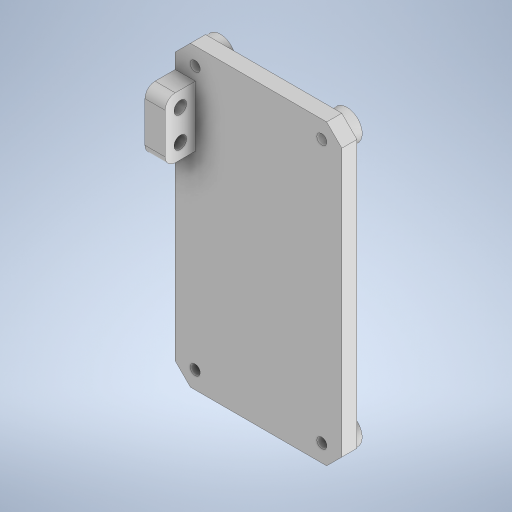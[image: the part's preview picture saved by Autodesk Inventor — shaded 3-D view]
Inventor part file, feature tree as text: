
AUTODESK INVENTOR PART (.ipt)
format: ipt  version: 2023 (Build 270158000, 158)  size: 288,256 bytes
history: native  units: mm
features: sketch x3, extrude x3, projected_geometry x3, other x1, hole x1, fillet x1, chamfer x1
ambient origin geometry x8: Origin, YZ Plane, XZ Plane, XY Plane, X Axis, Y Axis, Z Axis, Center Point
bodies: Body1 (feature_tree)
feature tree (13):
  other  "솔리드1"
  sketch  "스케치1"
  extrude  "돌출1"  Depth=33.0mm
  extrude  "돌출2"  Depth=59.0mm
  hole  "구멍1"  [1 undecoded]
  extrude  "돌출3"  Depth=57.6mm
  fillet  "모깎기1"  Radius=6.0mm
  chamfer  "모따기1"  Distance=25.1mm
  sketch  "스케치3"
  projected_geometry  "투영된 루프1"
  projected_geometry  "투영된 루프2"
  projected_geometry  "투영된 루프3"
  sketch  "스케치4"
note: 1 required parameter value undecoded (feature->parameter linkage not recoverable at this tier; creation-order binding heuristic only, values carry confidence <= 0.55)
